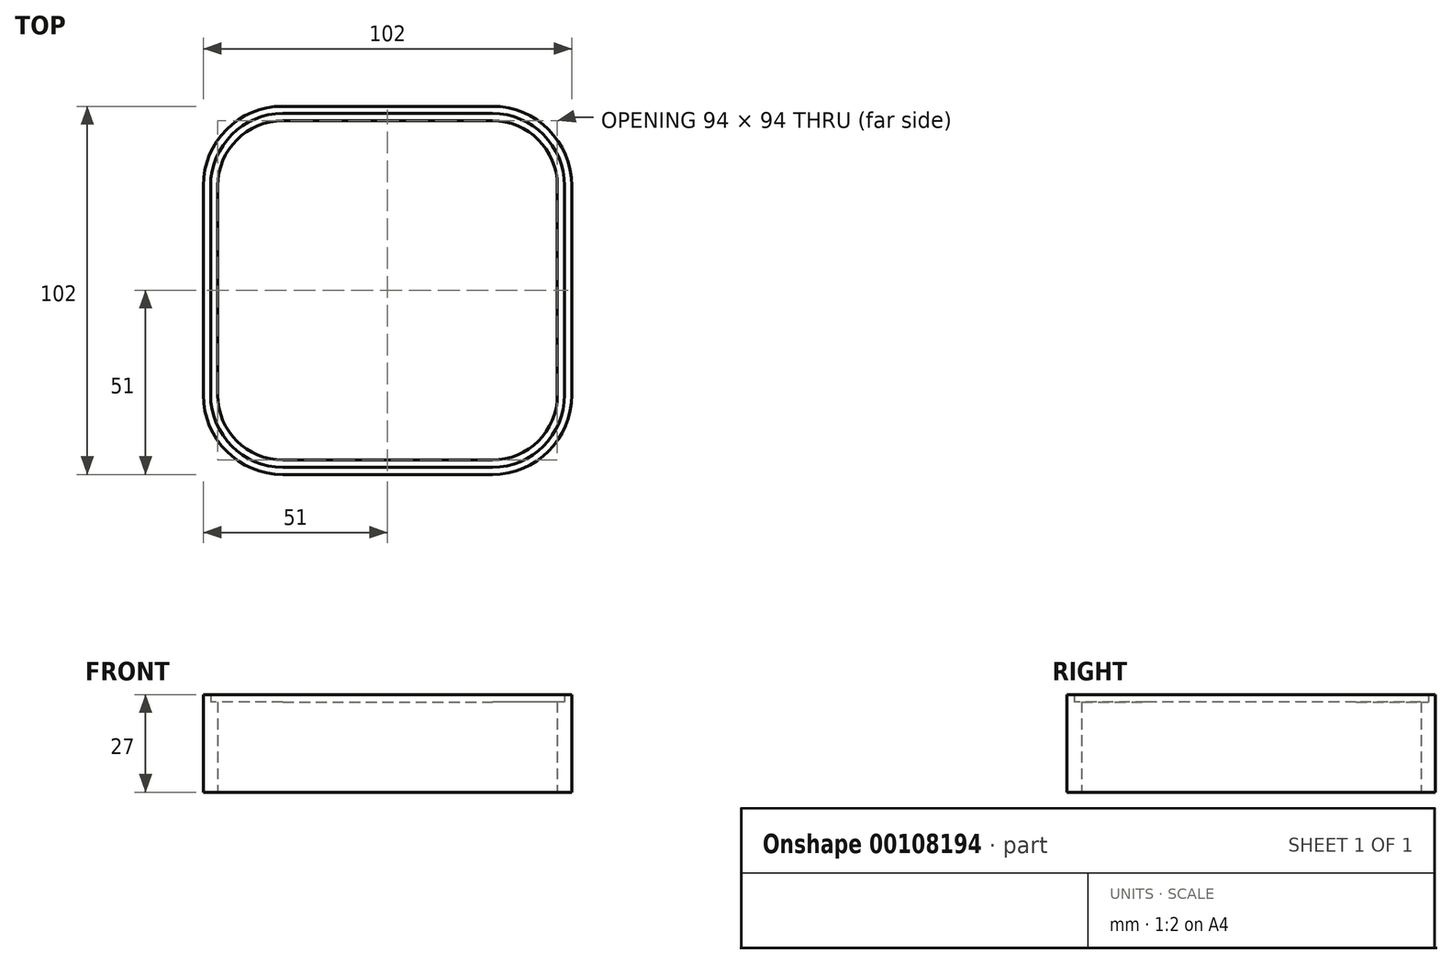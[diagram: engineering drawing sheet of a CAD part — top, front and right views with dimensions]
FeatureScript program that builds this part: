
annotation { "Feature Type Name" : "Feature", "Feature Type Description" : "" }
export const myFeature = defineFeature(function(context is Context, id is Id, definition is map)
    precondition{}
    {
        {
            var Q0;
            Q0=qCreatedBy(makeId("Top.planeOp"),FACE);
            var sketch = newSketch(context, id + "F0", { "sketchPlane" : qUnion([Q0])});
            skLineSegment(sketch, "E0.bottom", {"start": v(-29, 49) * mm, "end": v(29, 49) * mm});
            skLineSegment(sketch, "E0.top", {"start": v(-29, -49) * mm, "end": v(29, -49) * mm});
            skLineSegment(sketch, "E0.left", {"start": v(-49, 29) * mm, "end": v(-49, -29) * mm});
            skLineSegment(sketch, "E0.right", {"start": v(49, 29) * mm, "end": v(49, -29) * mm});
            skPoint(sketch, "E0.middle", {"position": v(0, 0) * mm});
            skPoint(sketch, "E1.visualSharp", {"position": v(-49, 49) * mm});
            skArc(sketch, "E1.filletArc", {"start": v(-29, 49) * mm, "mid": v(-43.14, 43.14) * mm, "end": v(-49, 29) * mm});
            skPoint(sketch, "E2.visualSharp", {"position": v(49, 49) * mm});
            skArc(sketch, "E2.filletArc", {"start": v(49, 29) * mm, "mid": v(43.14, 43.14) * mm, "end": v(29, 49) * mm});
            skPoint(sketch, "E3.visualSharp", {"position": v(49, -49) * mm});
            skArc(sketch, "E3.filletArc", {"start": v(29, -49) * mm, "mid": v(43.14, -43.14) * mm, "end": v(49, -29) * mm});
            skPoint(sketch, "E4.visualSharp", {"position": v(-49, -49) * mm});
            skArc(sketch, "E4.filletArc", {"start": v(-49, -29) * mm, "mid": v(-43.14, -43.14) * mm, "end": v(-29, -49) * mm});
            skLineSegment(sketch, "E5.0", {"start": v(-29, 51) * mm, "end": v(29, 51) * mm});
            skArc(sketch, "E5.1", {"start": v(51, 29) * mm, "mid": v(44.56, 44.56) * mm, "end": v(29, 51) * mm});
            skArc(sketch, "E5.2", {"start": v(-29, 51) * mm, "mid": v(-44.56, 44.56) * mm, "end": v(-51, 29) * mm});
            skLineSegment(sketch, "E5.3", {"start": v(51, 29) * mm, "end": v(51, -29) * mm});
            skLineSegment(sketch, "E5.4", {"start": v(-51, 29) * mm, "end": v(-51, -29) * mm});
            skArc(sketch, "E5.5", {"start": v(-51, -29) * mm, "mid": v(-44.56, -44.56) * mm, "end": v(-29, -51) * mm});
            skLineSegment(sketch, "E5.6", {"start": v(-29, -51) * mm, "end": v(29, -51) * mm});
            skArc(sketch, "E5.7", {"start": v(29, -51) * mm, "mid": v(44.56, -44.56) * mm, "end": v(51, -29) * mm});
            skLineSegment(sketch, "E6.0", {"start": v(-29, 47) * mm, "end": v(29, 47) * mm});
            skArc(sketch, "E6.1", {"start": v(47, 29) * mm, "mid": v(41.73, 41.73) * mm, "end": v(29, 47) * mm});
            skArc(sketch, "E6.2", {"start": v(-29, 47) * mm, "mid": v(-41.73, 41.73) * mm, "end": v(-47, 29) * mm});
            skLineSegment(sketch, "E6.3", {"start": v(47, 29) * mm, "end": v(47, -29) * mm});
            skLineSegment(sketch, "E6.4", {"start": v(-47, 29) * mm, "end": v(-47, -29) * mm});
            skArc(sketch, "E6.5", {"start": v(-47, -29) * mm, "mid": v(-41.73, -41.73) * mm, "end": v(-29, -47) * mm});
            skLineSegment(sketch, "E6.6", {"start": v(-29, -47) * mm, "end": v(29, -47) * mm});
            skArc(sketch, "E6.7", {"start": v(29, -47) * mm, "mid": v(41.73, -41.73) * mm, "end": v(47, -29) * mm});
            skSolve(sketch);
        }
        {
            var Q0;
            Q0=makeQuery(id+"F0.imprint","IMPRINT",FACE,{"disambiguationData":[TD([[makeQuery(id+"F0.imprint","IMPRINT",EDGE,{"derivedFrom":sQuery(id+"F0.wireOp",EDGE,"E0.bottom")}),-1.0]])]});
            extrude(context, id + "F1", {"entities" : qUnion([Q0]), "depth" : 25 * mm});
        }
        {
            var Q0;
            Q0=makeQuery(id+"F0.imprint","IMPRINT",FACE,{"disambiguationData":[TD([[makeQuery(id+"F0.imprint","IMPRINT",EDGE,{"derivedFrom":sQuery(id+"F0.wireOp",EDGE,"E0.bottom")}),1.0]])]});
            extrude(context, id + "F2", {"entities" : qUnion([Q0]), "operationType" : NewBodyOperationType.ADD, "depth" : 27 * mm});
        }
    });
